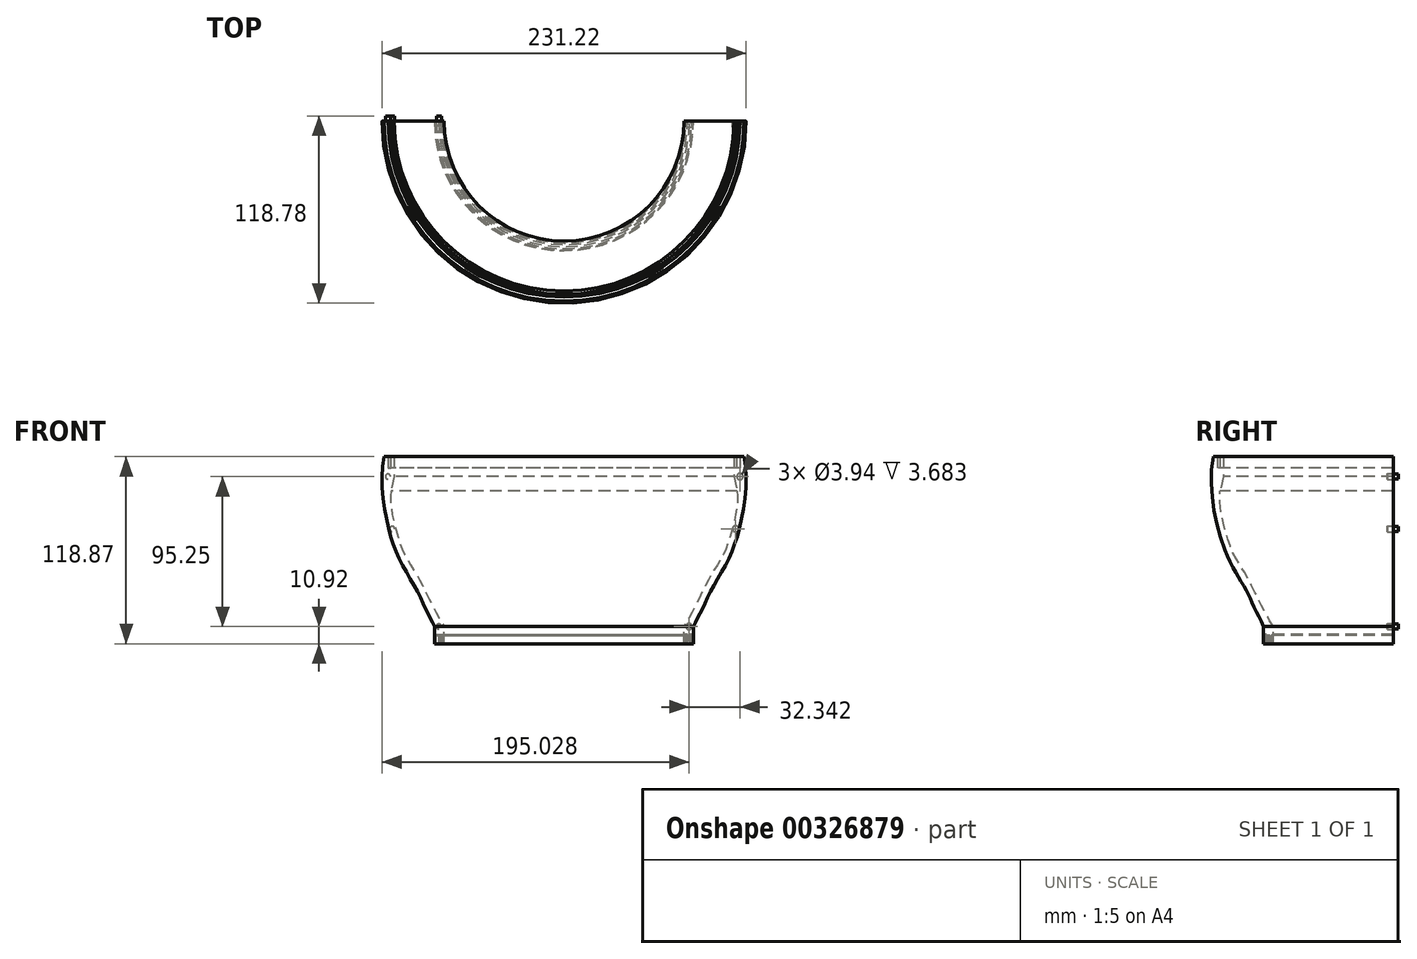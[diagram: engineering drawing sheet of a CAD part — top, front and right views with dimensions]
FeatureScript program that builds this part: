
annotation { "Feature Type Name" : "Feature", "Feature Type Description" : "" }
export const myFeature = defineFeature(function(context is Context, id is Id, definition is map)
    precondition{}
    {
        {
            var Q0;
            Q0=qCreatedBy(makeId("Front.planeOp"),FACE);
            var sketch = newSketch(context, id + "F0", { "sketchPlane" : qUnion([Q0])});
            skLineSegment(sketch, "E0", {"start": v(0, 0) * mm, "end": v(82.3, 0) * mm});
            skLineSegment(sketch, "E1", {"start": v(82.3, 0) * mm, "end": v(82.3, -5.08) * mm});
            skLineSegment(sketch, "E2", {"start": v(82.3, -5.08) * mm, "end": v(79.76, -5.08) * mm});
            skLineSegment(sketch, "E3", {"start": v(79.76, -5.08) * mm, "end": v(79.76, -10.92) * mm});
            skLineSegment(sketch, "E4", {"start": v(79.76, -10.92) * mm, "end": v(78.49, -10.92) * mm});
            skLineSegment(sketch, "E5", {"start": v(78.49, -10.92) * mm, "end": v(78.49, -5.08) * mm});
            skLineSegment(sketch, "E6", {"start": v(78.49, -5.08) * mm, "end": v(76.2, -5.08) * mm});
            skLineSegment(sketch, "E7", {"start": v(76.2, -5.08) * mm, "end": v(76.2, 0) * mm});
            skLineSegment(sketch, "E8", {"start": v(0, 0) * mm, "end": v(0, -6.62) * mm});
            skSolve(sketch);
        }
        {
            var Q0;
            Q0 = qSketchRegion(id + "F0", true);
            var Q1;
            Q1=sQuery(id+"F0.wireOp",EDGE,"E8");
            revolve(context, id + "F1", {"entities" : qUnion([Q0]), "axis" : qUnion([Q1]), "revolveType" : RevolveType.ONE_DIRECTION, "angle" : 180 * degree});
        }
        {
            var Q0;
            Q0=makeQuery(id+"F1.opRevolve","CAP_FACE",FACE,{"disambiguationData":[OSD([sQuery(id+"F0.wireOp",EDGE,"E0"),sQuery(id+"F0.wireOp",EDGE,"E1"),sQuery(id+"F0.wireOp",EDGE,"E2"),sQuery(id+"F0.wireOp",EDGE,"E3"),sQuery(id+"F0.wireOp",EDGE,"E4"),sQuery(id+"F0.wireOp",EDGE,"E5"),sQuery(id+"F0.wireOp",EDGE,"E6"),sQuery(id+"F0.wireOp",EDGE,"E7")])],"isStart":false});
            var sketch = newSketch(context, id + "F2", { "sketchPlane" : qUnion([Q0])});
            skLineSegment(sketch, "E9", {"start": v(0, 0) * mm, "end": v(0, 107.95) * mm});
            skLineSegment(sketch, "E10", {"start": v(0, 107.95) * mm, "end": v(109.98, 107.95) * mm});
            skFitSpline(sketch, "E11", {"points": [v(82.3, 0) * mm, v(86.43, 8.2) * mm, v(92.6, 21.34) * mm, v(103.55, 40.97) * mm, v(112.28, 65.92) * mm, v(114.3, 107.95) * mm], "startDerivative": vector(24.25, 63.12) * mm, "endDerivative": vector(-29.27, 138.23) * mm});
            skLineSegment(sketch, "E12", {"start": v(107.95, 107.95) * mm, "end": v(107.95, 95.44) * mm});
            skLineSegment(sketch, "E13", {"start": v(111.76, 107.95) * mm, "end": v(111.76, 100.75) * mm});
            skLineSegment(sketch, "E14", {"start": v(111.76, 100.75) * mm, "end": v(109.98, 100.75) * mm});
            skLineSegment(sketch, "E15", {"start": v(109.98, 100.75) * mm, "end": v(109.98, 107.95) * mm});
            skLineSegment(sketch, "E16", {"start": v(107.95, 95.44) * mm, "end": v(109.96, 86.05) * mm});
            skFitSpline(sketch, "E17", {"points": [v(109.96, 86.05) * mm, v(109.96, 76.9) * mm, v(105.8, 58.17) * mm, v(101.12, 45.6) * mm, v(95.16, 35.6) * mm, v(89.3, 24.82) * mm, v(80.84, 8.2) * mm, v(76.2, 0) * mm], "startDerivative": vector(6.44, -70.7) * mm, "endDerivative": vector(-34.53, -59.23) * mm});
            skLineSegment(sketch, "E18", {"start": v(76.2, 0) * mm, "end": v(82.3, 0) * mm});
            skLineSegment(sketch, "E19.trimOffspring", {"start": v(111.76, 107.95) * mm, "end": v(114.3, 107.95) * mm});
            skSolve(sketch);
        }
        {
            var Q0;
            Q0 = qSketchRegion(id + "F2", true);
            var Q1;
            Q1=sQuery(id+"F2.wireOp",EDGE,"E9");
            revolve(context, id + "F3", {"operationType" : NewBodyOperationType.ADD, "entities" : qUnion([Q0]), "axis" : qUnion([Q1]), "revolveType" : RevolveType.ONE_DIRECTION, "angle" : 180 * degree});
        }
        {
            var Q0;
            Q0=makeQuery(id+"F3.boolean.opBoolean","MERGE",FACE,{"derivedFrom":[makeQuery(id+"F1.opRevolve","CAP_FACE",FACE,{"disambiguationData":[OSD([sQuery(id+"F0.wireOp",EDGE,"E0"),sQuery(id+"F0.wireOp",EDGE,"E1"),sQuery(id+"F0.wireOp",EDGE,"E2"),sQuery(id+"F0.wireOp",EDGE,"E3"),sQuery(id+"F0.wireOp",EDGE,"E4"),sQuery(id+"F0.wireOp",EDGE,"E5"),sQuery(id+"F0.wireOp",EDGE,"E6"),sQuery(id+"F0.wireOp",EDGE,"E7")])],"isStart":false}),makeQuery(id+"F3.opRevolve","CAP_FACE",FACE,{"disambiguationData":[OSD([sQuery(id+"F2.wireOp",EDGE,"E10"),sQuery(id+"F2.wireOp",EDGE,"E11"),sQuery(id+"F2.wireOp",EDGE,"E12"),sQuery(id+"F2.wireOp",EDGE,"E13"),sQuery(id+"F2.wireOp",EDGE,"E14"),sQuery(id+"F2.wireOp",EDGE,"E15"),sQuery(id+"F2.wireOp",EDGE,"E16"),sQuery(id+"F2.wireOp",EDGE,"E17"),sQuery(id+"F2.wireOp",EDGE,"E18"),sQuery(id+"F2.wireOp",EDGE,"E19.trimOffspring")])],"isStart":true})]});
            var sketch = newSketch(context, id + "F4", { "sketchPlane" : qUnion([Q0])});
            skSolve(sketch);
        }
        {
            var Q0;
            Q0=makeQuery(id+"F4.imprint","IMPRINT",FACE,{"disambiguationData":[TD([[makeQuery(id+"F4.imprint","IMPRINT",EDGE,{"derivedFrom":makeQuery(id+"F1.opRevolve","CAP_EDGE",EDGE,{"disambiguationData":[OSD([sQuery(id+"F0.wireOp",EDGE,"E1")])],"isStart":false})}),-1.0]])]});
            var sketch = newSketch(context, id + "F5", { "sketchPlane" : qUnion([Q0])});
            skCircle(sketch, "E20", {"center": v(111.76, 95.25) * mm, "radius": 1.59 * mm});
            skCircle(sketch, "E21", {"center": v(79.46, 0) * mm, "radius": 1.59 * mm});
            skCircle(sketch, "E22", {"center": v(109.08, 62.03) * mm, "radius": 1.59 * mm});
            skCircle(sketch, "E23.MirrorC", {"center": v(-111.76, 95.25) * mm, "radius": 1.59 * mm});
            skCircle(sketch, "E24.MirrorC", {"center": v(-109.08, 62.03) * mm, "radius": 1.59 * mm});
            skCircle(sketch, "E25.MirrorC", {"center": v(-79.46, 0) * mm, "radius": 1.59 * mm});
            skSolve(sketch);
        }
        {
            var Q0;
            Q0 = qSketchRegion(id + "F5", true);
            extrude(context, id + "F6", {"entities" : qUnion([Q0]), "operationType" : NewBodyOperationType.ADD, "depth" : 3.17 * mm});
        }
        {
            var Q0;
            Q0=makeQuery(id+"F6.opExtrude","CAP_FACE",FACE,{"disambiguationData":[OSD([sQuery(id+"F5.wireOp",EDGE,"E23.MirrorC")])],"isStart":false});
            var sketch = newSketch(context, id + "F7", { "sketchPlane" : qUnion([Q0])});
            skCircle(sketch, "E26", {"center": v(-111.76, 95.25) * mm, "radius": 1.97 * mm});
            skCircle(sketch, "E27", {"center": v(-109.07, 62.06) * mm, "radius": 1.97 * mm});
            skCircle(sketch, "E28", {"center": v(-79.42, 0) * mm, "radius": 1.97 * mm});
            skSolve(sketch);
        }
        {
            var Q0;
            Q0 = qSketchRegion(id + "F7", true);
            extrude(context, id + "F8", {"entities" : qUnion([Q0]), "operationType" : NewBodyOperationType.REMOVE, "oppositeDirection" : true, "depth" : 6.86 * mm});
        }
        {
            var Q0;
            Q0=makeQuery(id+"F3.boolean.opBoolean","MERGE",FACE,{"derivedFrom":[makeQuery(id+"F1.opRevolve","CAP_FACE",FACE,{"disambiguationData":[OSD([sQuery(id+"F0.wireOp",EDGE,"E0"),sQuery(id+"F0.wireOp",EDGE,"E1"),sQuery(id+"F0.wireOp",EDGE,"E2"),sQuery(id+"F0.wireOp",EDGE,"E3"),sQuery(id+"F0.wireOp",EDGE,"E4"),sQuery(id+"F0.wireOp",EDGE,"E5"),sQuery(id+"F0.wireOp",EDGE,"E6"),sQuery(id+"F0.wireOp",EDGE,"E7")])],"isStart":true}),makeQuery(id+"F3.opRevolve","CAP_FACE",FACE,{"disambiguationData":[OSD([sQuery(id+"F2.wireOp",EDGE,"E10"),sQuery(id+"F2.wireOp",EDGE,"E11"),sQuery(id+"F2.wireOp",EDGE,"E12"),sQuery(id+"F2.wireOp",EDGE,"E13"),sQuery(id+"F2.wireOp",EDGE,"E14"),sQuery(id+"F2.wireOp",EDGE,"E15"),sQuery(id+"F2.wireOp",EDGE,"E16"),sQuery(id+"F2.wireOp",EDGE,"E17"),sQuery(id+"F2.wireOp",EDGE,"E18"),sQuery(id+"F2.wireOp",EDGE,"E19.trimOffspring")])],"isStart":false})]});
            var sketch = newSketch(context, id + "F9", { "sketchPlane" : qUnion([Q0])});
            skLineSegment(sketch, "E29", {"start": v(-82.3, -5.08) * mm, "end": v(-82.3, -10.92) * mm});
            skLineSegment(sketch, "E30", {"start": v(-82.3, -10.92) * mm, "end": v(-81.1, -10.92) * mm});
            skLineSegment(sketch, "E31", {"start": v(-81.1, -10.92) * mm, "end": v(-81.1, -5.73) * mm});
            skLineSegment(sketch, "E32", {"start": v(-82.3, -5.08) * mm, "end": v(-81.9, -5.08) * mm});
            skLineSegment(sketch, "E33", {"start": v(-81.9, -5.08) * mm, "end": v(-81.1, -5.73) * mm});
            skLineSegment(sketch, "E34", {"start": v(-76.2, -5.08) * mm, "end": v(-76.2, -10.92) * mm});
            skLineSegment(sketch, "E35", {"start": v(-76.2, -10.92) * mm, "end": v(-77.4, -10.92) * mm});
            skLineSegment(sketch, "E36", {"start": v(-77.4, -10.92) * mm, "end": v(-77.4, -5.68) * mm});
            skLineSegment(sketch, "E37", {"start": v(-77.4, -5.68) * mm, "end": v(-76.6, -5.08) * mm});
            skLineSegment(sketch, "E38", {"start": v(-76.6, -5.08) * mm, "end": v(-76.2, -5.08) * mm});
            skLineSegment(sketch, "E39", {"start": v(0, 0) * mm, "end": v(0, -15.3) * mm});
            skSolve(sketch);
        }
        {
            var Q0;
            Q0 = qSketchRegion(id + "F9", true);
            var Q1;
            Q1=sQuery(id+"F9.wireOp",EDGE,"E39");
            revolve(context, id + "F10", {"operationType" : NewBodyOperationType.ADD, "entities" : qUnion([Q0]), "axis" : qUnion([Q1]), "revolveType" : RevolveType.ONE_DIRECTION, "angle" : 180 * degree});
        }
    });
